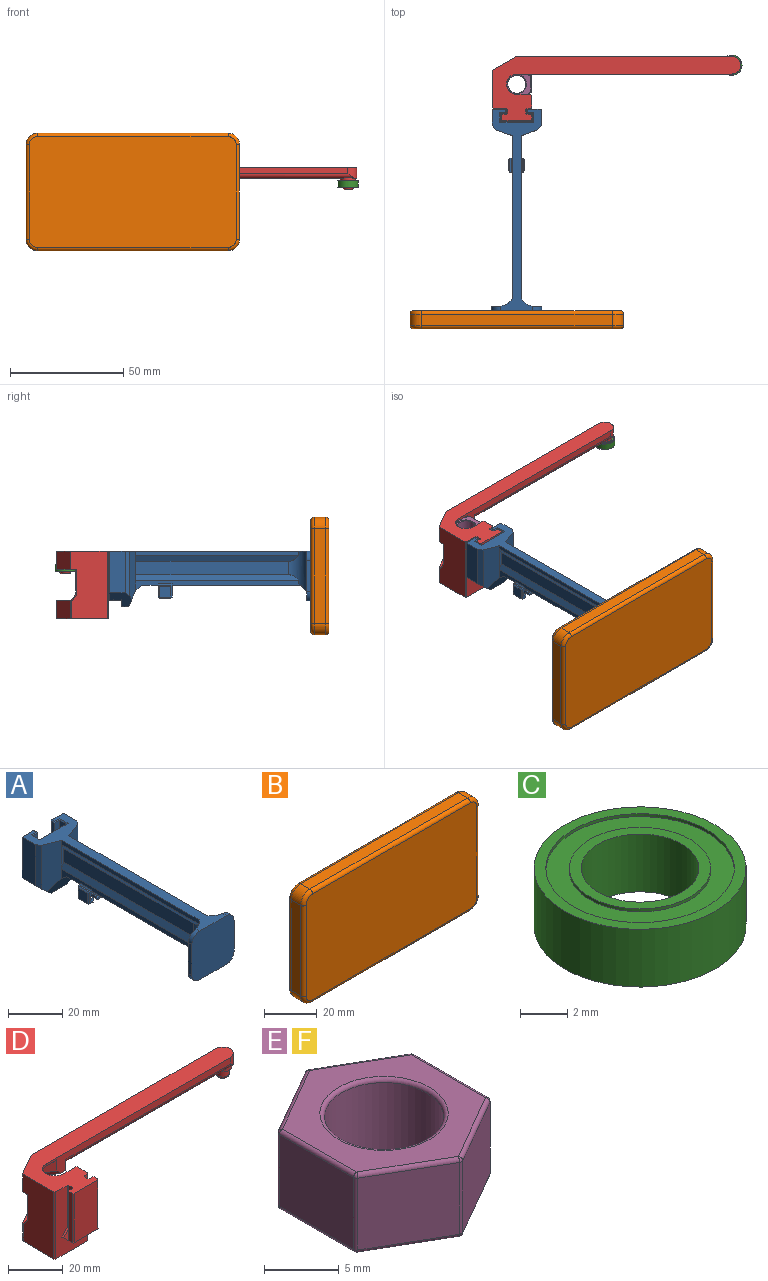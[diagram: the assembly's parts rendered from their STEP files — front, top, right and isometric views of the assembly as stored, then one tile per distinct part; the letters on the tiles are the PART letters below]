
ASSEMBLY  parts=6 mates=3
PART A: 121 faces, bbox 22x89x24.5 mm
  f0: plane 6.2x5.8mm, normal (0,1,0), area 14mm2, adj f3,f5,f7,f45,f47,f65,f70,f75
  f1: plane 6.2x5.8mm, normal (0,-1,0), area 14mm2, adj f2,f3,f5,f45,f47,f68,f73,f78
  f2: plane 57.05x5.58mm, normal (0,0,-1), area 228.9mm2, adj f1,f3,f5,f62,f63,f115
  f3: plane 72.07x4.42mm, normal (-1,0,0), area 139.2mm2, adj f0,f1,f2,f7,f13,f41,f62,f114
  f4: plane 72.07x1.92mm, normal (-1,0,0), area 138.5mm2, adj f10,f13,f40,f62
  f5: plane 72.07x4.42mm, normal (1,0,0), area 139.2mm2, adj f0,f1,f2,f7,f14,f38,f63,f113
  f6: plane 72.07x1.92mm, normal (1,0,0), area 138.5mm2, adj f10,f14,f39,f63
  f7: plane 7x4mm, normal (0,0,-1), area 28mm2, adj f0,f3,f5,f116
  f8: plane 11.16x1.4mm, normal (0,-1,0), area 12mm2, adj f13,f29,f40,f41
  f9: plane 21.83x6.44mm, normal (0,1,0), area 130.2mm2, adj f10,f12,f22,f26,f37,f118
  f10: plane 89.02x21.6mm, normal (0,0,1), area 483.4mm2, adj f4,f6,f9,f11,f12,f13,f14,f15
  f11: plane 21.83x6.44mm, normal (0,1,0), area 130.2mm2, adj f10,f15,f18,f25,f31,f117
  f12: plane 18.5x6.97mm, normal (-1,0,0), area 129mm2, adj f9,f10,f118,f120
  f13: plane 21.68x7.39mm, normal (-0.34,-0.94,0), area 156.6mm2, adj f3,f4,f8,f10,f64,f118,f120
  f14: plane 21.68x7.39mm, normal (0.34,-0.94,0), area 156.6mm2, adj f5,f6,f10,f27,f64,f117,f119
  f15: plane 18.5x6.97mm, normal (1,0,0), area 129mm2, adj f10,f11,f117,f119
  f16: plane 8.2x3.05mm, normal (0,0,-1), area 25mm2, adj f19,f64,f117,f118
  f17: plane 22x22mm, normal (0,-1,0), area 470.3mm2, adj f10,f42,f43,f44,f58,f59,f60,f61
  f18: plane 5.42x3mm, normal (-0.74,0,-0.67), area 7.4mm2, adj f11,f19,f23,f24,f25,f117
  f19: plane 24.1x14.17mm, normal (0,1,0), area 333mm2, adj f16,f18,f21,f23,f26,f34,f117,f118
  f20: plane 21.41x2.71mm, normal (0,-1,0), area 54mm2, adj f21,f22,f26,f36
  f21: plane 21.41x3.61mm, normal (1,0,0), area 77.3mm2, adj f19,f20,f26,f35
  f22: plane 18.43x1.81mm, normal (1,0,0), area 33.4mm2, adj f9,f20,f26,f37
  f23: plane 21.41x3.61mm, normal (-1,0,0), area 77.3mm2, adj f18,f19,f24,f33
  f24: plane 21.41x2.71mm, normal (0,-1,0), area 54mm2, adj f18,f23,f25,f32
  f25: plane 18.43x1.81mm, normal (-1,0,0), area 33.4mm2, adj f11,f18,f24,f31
  f26: plane 5.42x3mm, normal (0.74,0,-0.67), area 7.4mm2, adj f9,f19,f20,f21,f22,f118
  f27: plane 11.16x1.4mm, normal (0,-1,0), area 12mm2, adj f14,f30,f38,f39
  f28: plane 22x21.67mm, normal (0,1,0), area 161mm2, adj f42,f43,f44,f58,f59,f60,f61,f62
  f29: plane 67.55x6mm, normal (-1,0,0), area 405.3mm2, adj f8,f40,f41,f62
  f30: plane 67.55x6mm, normal (1,0,0), area 405.3mm2, adj f27,f38,f39,f63
  f31: plane 1.81x0.4mm, normal (-0.71,0,0.71), area 0.9mm2, adj f10,f11,f25,f32
  f32: plane 3.11x0.4mm, normal (0,-0.71,0.71), area 1.5mm2, adj f10,f24,f31,f33
  f33: plane 4.41x0.4mm, normal (-0.71,0,0.71), area 2.3mm2, adj f10,f23,f32,f34
  f34: plane 14.94x0.4mm, normal (0,0.71,0.71), area 8.2mm2, adj f10,f19,f33,f35
  f35: plane 4.41x0.4mm, normal (0.71,0,0.71), area 2.3mm2, adj f10,f21,f34,f36
  f36: plane 3.11x0.4mm, normal (0,-0.71,0.71), area 1.5mm2, adj f10,f20,f35,f37
  f37: plane 1.81x0.4mm, normal (0.71,0,0.71), area 0.9mm2, adj f9,f10,f22,f36
  f38: plane 72.07x2.58mm, normal (0.88,0,0.48), area 207.2mm2, adj f5,f27,f30,f63
  f39: plane 72.07x2.58mm, normal (0.88,0,-0.48), area 207.2mm2, adj f6,f27,f30,f63
  f40: plane 72.07x2.58mm, normal (-0.88,0,-0.48), area 207.2mm2, adj f4,f8,f29,f62
  f41: plane 72.07x2.58mm, normal (-0.88,0,0.48), area 207.2mm2, adj f3,f8,f29,f62
  f42: plane 14x1.8mm, normal (0,0,-1), area 25.2mm2, adj f17,f28,f59,f61
  f43: plane 14x1.8mm, normal (1,0,0), area 25.2mm2, adj f17,f28,f60,f61
  f44: plane 14x1.8mm, normal (-1,0,0), area 25.2mm2, adj f17,f28,f58,f59
  f45: plane 6x0.6mm, normal (0,0,1), area 3.6mm2, adj f0,f1,f66,f113
  f46: plane 5x4.8mm, normal (1,0,0), area 24mm2, adj f65,f66,f68,f69
  f47: plane 6x0.6mm, normal (0,0,1), area 3.6mm2, adj f0,f1,f90,f114
  f48: plane 5x4.8mm, normal (-1,0,0), area 24mm2, adj f85,f90,f95,f96
  f49: plane 5x1.75mm, normal (0,0,-1), area 8.8mm2, adj f94,f95,f105,f106
  f50: plane 5x1mm, normal (1,0,0), area 5mm2, adj f51,f93,f105,f111
  f51: plane 5x0.75mm, normal (0,0,1), area 3.8mm2, adj f50,f100,f108,f112
  f52: plane 5x1.8mm, normal (1,0,0), area 9mm2, adj f98,f99,f107,f108
  f53: plane 5x3.2mm, normal (0,0,-1), area 16mm2, adj f87,f88,f97,f98
  f54: plane 5x1.8mm, normal (-1,0,0), area 9mm2, adj f81,f82,f86,f87
  f55: plane 5x0.75mm, normal (0,0,1), area 3.8mm2, adj f56,f77,f80,f81
  f56: plane 5x1mm, normal (-1,0,0), area 5mm2, adj f55,f74,f75,f78
  f57: plane 5x1.75mm, normal (0,0,-1), area 8.8mm2, adj f69,f70,f73,f74
  f58: cylinder r=4mm len=4mm, axis (0,1,0), area 11.4mm2, adj f10,f17,f28,f44,f62
  f59: cylinder r=4mm len=4mm, axis (0,1,0), area 11.3mm2, adj f17,f28,f42,f44
  f60: cylinder r=4mm len=4mm, axis (0,-1,0), area 11.4mm2, adj f10,f17,f28,f43,f63
  f61: cylinder r=4mm len=4mm, axis (0,-1,0), area 11.3mm2, adj f17,f28,f42,f43
  f62: cylinder r=8mm len=18mm, axis (0,0,-1), area 166.3mm2, adj f2,f3,f4,f10,f28,f29,f40,f41
  f63: cylinder r=8mm len=18mm, axis (0,0,1), area 166.3mm2, adj f2,f5,f6,f10,f28,f30,f38,f39
  f64: plane 14.5x7mm, normal (0,-0.91,-0.42), area 77.7mm2, adj f13,f14,f16,f116,f117,f118
  f65: plane 5.3x0.5mm, normal (0.71,0.71,0), area 3.6mm2, adj f0,f46,f66,f67
  f66: plane 6x0.5mm, normal (0.71,0,0.71), area 3.9mm2, adj f45,f46,f65,f68
  f67: plane 0.5x0.5mm, normal (0.58,0.58,-0.58), area 0.2mm2, adj f65,f69,f70
  f68: plane 5.3x0.5mm, normal (0.71,-0.71,0), area 3.6mm2, adj f1,f46,f66,f71
  f69: plane 5x0.5mm, normal (0.71,0,-0.71), area 3.5mm2, adj f46,f57,f67,f71
  f70: plane 1.75x0.5mm, normal (0,0.71,-0.71), area 1.2mm2, adj f0,f57,f67,f72
  f71: plane 0.5x0.5mm, normal (0.58,-0.58,-0.58), area 0.2mm2, adj f68,f69,f73
  f72: plane 0.5x0.5mm, normal (-0.58,0.58,-0.58), area 0.2mm2, adj f70,f74,f75
  f73: plane 1.75x0.5mm, normal (0,-0.71,-0.71), area 1.2mm2, adj f1,f57,f71,f76
  f74: plane 5x0.5mm, normal (-0.71,0,-0.71), area 3.5mm2, adj f56,f57,f72,f76
  f75: plane 1x0.5mm, normal (-0.71,0.71,0), area 0.5mm2, adj f0,f56,f72,f77
  f76: plane 0.5x0.5mm, normal (-0.58,-0.58,-0.58), area 0.2mm2, adj f73,f74,f78
  f77: plane 0.75x0.5mm, normal (0,0.71,0.71), area 0.4mm2, adj f0,f55,f75,f79
  f78: plane 1x0.5mm, normal (-0.71,-0.71,0), area 0.5mm2, adj f1,f56,f76,f80
  f79: plane 1x1mm, normal (-0.58,0.58,0.58), area 0.6mm2, adj f0,f77,f81,f82
  f80: plane 0.75x0.5mm, normal (0,-0.71,0.71), area 0.4mm2, adj f1,f55,f78,f83
  f81: plane 5x0.5mm, normal (-0.71,0,0.71), area 3.5mm2, adj f54,f55,f79,f83
  f82: plane 1.8x0.5mm, normal (-0.71,0.71,0), area 1.3mm2, adj f0,f54,f79,f84
  f83: plane 1x1mm, normal (-0.58,-0.58,0.58), area 0.6mm2, adj f1,f80,f81,f86
  f84: plane 1x1mm, normal (-0.58,0.58,-0.58), area 0.6mm2, adj f0,f82,f87,f88
  f85: plane 5.3x0.5mm, normal (-0.71,0.71,0), area 3.6mm2, adj f0,f48,f89,f90
  f86: plane 1.8x0.5mm, normal (-0.71,-0.71,0), area 1.3mm2, adj f1,f54,f83,f91
  f87: plane 5x0.5mm, normal (-0.71,0,-0.71), area 3.5mm2, adj f53,f54,f84,f91
  f88: plane 3.2x0.5mm, normal (0,0.71,-0.71), area 2.3mm2, adj f0,f53,f84,f92
  f89: plane 0.5x0.5mm, normal (-0.58,0.58,-0.58), area 0.2mm2, adj f85,f94,f95
  f90: plane 6x0.5mm, normal (-0.71,0,0.71), area 3.9mm2, adj f47,f48,f85,f96
  f91: plane 1x1mm, normal (-0.58,-0.58,-0.58), area 0.6mm2, adj f1,f86,f87,f97
  f92: plane 1x1mm, normal (0.58,0.58,-0.58), area 0.6mm2, adj f0,f88,f98,f99
  f93: plane 1x0.5mm, normal (0.71,0.71,0), area 0.5mm2, adj f0,f50,f100,f101
  f94: plane 1.75x0.5mm, normal (0,0.71,-0.71), area 1.2mm2, adj f0,f49,f89,f101
  f95: plane 5x0.5mm, normal (-0.71,0,-0.71), area 3.5mm2, adj f48,f49,f89,f102
  f96: plane 5.3x0.5mm, normal (-0.71,-0.71,0), area 3.6mm2, adj f1,f48,f90,f102
  f97: plane 3.2x0.5mm, normal (0,-0.71,-0.71), area 2.3mm2, adj f1,f53,f91,f103
  f98: plane 5x0.5mm, normal (0.71,0,-0.71), area 3.5mm2, adj f52,f53,f92,f103
  f99: plane 1.8x0.5mm, normal (0.71,0.71,0), area 1.3mm2, adj f0,f52,f92,f104
  f100: plane 0.75x0.5mm, normal (0,0.71,0.71), area 0.4mm2, adj f0,f51,f93,f104
  f101: plane 0.5x0.5mm, normal (0.58,0.58,-0.58), area 0.2mm2, adj f93,f94,f105
  f102: plane 0.5x0.5mm, normal (-0.58,-0.58,-0.58), area 0.2mm2, adj f95,f96,f106
  f103: plane 1x1mm, normal (0.58,-0.58,-0.58), area 0.6mm2, adj f1,f97,f98,f107
  f104: plane 1x1mm, normal (0.58,0.58,0.58), area 0.6mm2, adj f0,f99,f100,f108
  f105: plane 5x0.5mm, normal (0.71,0,-0.71), area 3.5mm2, adj f49,f50,f101,f109
  f106: plane 1.75x0.5mm, normal (0,-0.71,-0.71), area 1.2mm2, adj f1,f49,f102,f109
  f107: plane 1.8x0.5mm, normal (0.71,-0.71,0), area 1.3mm2, adj f1,f52,f103,f110
  f108: plane 5x0.5mm, normal (0.71,0,0.71), area 3.5mm2, adj f51,f52,f104,f110
  f109: plane 0.5x0.5mm, normal (0.58,-0.58,-0.58), area 0.2mm2, adj f105,f106,f111
  f110: plane 1x1mm, normal (0.58,-0.58,0.58), area 0.6mm2, adj f1,f107,f108,f112
  f111: plane 1x0.5mm, normal (0.71,-0.71,0), area 0.5mm2, adj f1,f50,f109,f112
  f112: plane 0.75x0.5mm, normal (0,-0.71,0.71), area 0.4mm2, adj f1,f51,f110,f111
  f113: plane 6x0.5mm, normal (0.71,0,0.71), area 4.2mm2, adj f0,f1,f5,f45
  f114: plane 6x0.5mm, normal (-0.71,0,0.71), area 4.2mm2, adj f0,f1,f3,f47
  f115: plane 17.2x3mm, normal (0,0.77,-0.64), area 35.8mm2, adj f2,f28,f62,f63
  f116: plane 4x3mm, normal (0,-0.64,-0.77), area 15.6mm2, adj f3,f5,f7,f64
  f117: plane 9.76x6.7mm, normal (0.67,0,-0.74), area 58.8mm2, adj f11,f14,f15,f16,f18,f19,f64,f119
  f118: plane 9.76x6.7mm, normal (-0.67,0,-0.74), area 58.8mm2, adj f9,f12,f13,f16,f19,f26,f64,f120
  f119: plane 19.76x2.01mm, normal (0.82,-0.57,0), area 47mm2, adj f10,f14,f15,f117
  f120: plane 19.76x2.01mm, normal (-0.82,-0.57,0), area 47mm2, adj f10,f12,f13,f118
PART B: 26 faces, bbox 95.2x8x52.8 mm
  f0: plane 84.38x5mm, normal (0,0,-1), area 421.9mm2, adj f6,f9,f15,f24
  f1: plane 41.96x5mm, normal (1,0,0), area 209.8mm2, adj f6,f7,f16,f23
  f2: plane 84.38x5mm, normal (0,0,1), area 421.9mm2, adj f7,f8,f12,f19
  f3: plane 41.96x5mm, normal (-1,0,0), area 209.8mm2, adj f8,f9,f11,f20
  f4: plane 91.38x48.96mm, normal (0,-1,0), area 4463.7mm2, adj f10,f11,f12,f13,f14,f15,f16,f17
  f5: plane 91.38x48.96mm, normal (0,1,0), area 4463.7mm2, adj f18,f19,f20,f21,f22,f23,f24,f25
  f6: cylinder r=5mm len=5mm, axis (0,-1,0), area 39.3mm2, adj f0,f1,f17,f25
  f7: cylinder r=5mm len=5mm, axis (0,1,0), area 39.3mm2, adj f1,f2,f14,f21
  f8: cylinder r=5mm len=5mm, axis (0,-1,0), area 39.3mm2, adj f2,f3,f10,f18
  f9: cylinder r=5mm len=5mm, axis (0,1,0), area 39.3mm2, adj f0,f3,f13,f22
  f10: torus R=3.5mm, axis (0,-1,0), area 16.5mm2, adj f4,f8,f11,f12
  f11: cylinder r=1.5mm len=41.96mm, axis (0,0,1), area 98.9mm2, adj f3,f4,f10,f13
  f12: cylinder r=1.5mm len=84.38mm, axis (1,0,0), area 198.8mm2, adj f2,f4,f10,f14
  f13: torus R=3.5mm, axis (0,-1,0), area 16.5mm2, adj f4,f9,f11,f15
  f14: torus R=3.5mm, axis (0,-1,0), area 16.5mm2, adj f4,f7,f12,f16
  f15: cylinder r=1.5mm len=84.38mm, axis (-1,0,0), area 198.8mm2, adj f0,f4,f13,f17
  f16: cylinder r=1.5mm len=41.96mm, axis (0,0,-1), area 98.9mm2, adj f1,f4,f14,f17
  f17: torus R=3.5mm, axis (0,-1,0), area 16.5mm2, adj f4,f6,f15,f16
  f18: torus R=3.5mm, axis (0,-1,0), area 16.5mm2, adj f5,f8,f19,f20
  f19: cylinder r=1.5mm len=84.38mm, axis (-1,0,0), area 198.8mm2, adj f2,f5,f18,f21
  f20: cylinder r=1.5mm len=41.96mm, axis (0,0,-1), area 98.9mm2, adj f3,f5,f18,f22
  f21: torus R=3.5mm, axis (0,-1,0), area 16.5mm2, adj f5,f7,f19,f23
  f22: torus R=3.5mm, axis (0,-1,0), area 16.5mm2, adj f5,f9,f20,f24
  f23: cylinder r=1.5mm len=41.96mm, axis (0,0,1), area 98.9mm2, adj f1,f5,f21,f25
  f24: cylinder r=1.5mm len=84.38mm, axis (1,0,0), area 198.8mm2, adj f0,f5,f22,f25
  f25: torus R=3.5mm, axis (0,-1,0), area 16.5mm2, adj f5,f6,f23,f24
PART C: 12 faces, bbox 9x9x3 mm
  f0: plane 8x8mm, normal (0,0,1), area 22mm2, adj f3,f9
  f1: plane 8x8mm, normal (0,0,-1), area 22mm2, adj f2,f7
  f2: cylinder r=4mm len=8mm, axis (0,0,-1), area 3.8mm2, adj f1,f6
  f3: cylinder r=4mm len=8mm, axis (0,0,-1), area 3.8mm2, adj f0,f5
  f4: cylinder r=4.5mm len=9mm, axis (0,0,-1), area 84.8mm2, adj f5,f6
  f5: plane 9x9mm, normal (0,0,1), area 13.4mm2, adj f3,f4
  f6: plane 9x9mm, normal (0,0,-1), area 13.4mm2, adj f2,f4
  f7: cylinder r=3mm len=6mm, axis (0,0,-1), area 2.8mm2, adj f1,f11
  f8: cylinder r=2.5mm len=5mm, axis (0,0,-1), area 47.1mm2, adj f10,f11
  f9: cylinder r=3mm len=6mm, axis (0,0,-1), area 2.8mm2, adj f0,f10
  f10: plane 6x6mm, normal (0,0,1), area 8.6mm2, adj f8,f9
  f11: plane 6x6mm, normal (0,0,-1), area 8.6mm2, adj f7,f8
PART D: 102 faces, bbox 109.6x28.3x30 mm
  f0: plane 30x16.3mm, normal (0,-1,0), area 252mm2, adj f1,f8,f62,f79,f80,f84,f93
  f1: plane 22.76x17.3mm, normal (0,0,-1), area 156.5mm2, adj f0,f3,f4,f23,f24,f25,f34,f35
  f2: plane 22x13.28mm, normal (0,-1,0), area 269.7mm2, adj f5,f6,f8,f62,f86,f87
  f3: plane 30x16.26mm, normal (-1,0,0), area 448.7mm2, adj f1,f8,f11,f18,f29,f84,f90,f91
  f4: plane 30x5.11mm, normal (1,0,0), area 88mm2, adj f1,f8,f29,f66,f67,f68,f69,f93
  f5: plane 5.91x3mm, normal (0.74,0,0.67), area 11.2mm2, adj f2,f42,f43,f44,f48,f62,f81,f82
  f6: plane 4.92x3mm, normal (-0.74,0,0.67), area 9.2mm2, adj f2,f45,f46,f47,f62,f80,f83,f85
  f7: plane 7.27x3.68mm, normal (1,0,0), area 12.9mm2, adj f18,f53,f61,f89,f101
  f8: plane 109.64x28.32mm, normal (0,0,1), area 1042.1mm2, adj f0,f2,f3,f4,f11,f17,f19,f20
  f9: plane 17.5x6.65mm, normal (0.5,0.87,0), area 134.4mm2, adj f10,f12,f21,f50
  f10: plane 17.5x7.68mm, normal (1,0,0), area 128.9mm2, adj f9,f15,f18,f21,f51,f92
  f11: plane 10.65x8mm, normal (-0.5,0.87,0), area 98.4mm2, adj f3,f8,f18,f55
  f12: plane 17.5x6.15mm, normal (0,1,0), area 107.6mm2, adj f9,f21,f49,f67
  f13: plane 6.65x4.72mm, normal (0.5,0.87,0), area 34.6mm2, adj f14,f31,f33,f38,f76,f78
  f14: plane 7.68x4.72mm, normal (1,0,0), area 34.6mm2, adj f13,f28,f33,f37,f77,f78
  f15: plane 7.34x6.5mm, normal (0.5,-0.87,0), area 50.5mm2, adj f10,f16,f18,f21,f74
  f16: plane 5.62x5.51mm, normal (-0.5,-0.87,0), area 29mm2, adj f15,f17,f21,f41,f73,f74
  f17: plane 95.09x8mm, normal (0,-1,0), area 295.5mm2, adj f8,f16,f18,f20,f41,f54,f73,f89
  f18: plane 21.3x8.96mm, normal (0,0,-1), area 79.4mm2, adj f3,f7,f10,f11,f15,f17,f22,f41
  f19: plane 6.15x1mm, normal (0,1,0), area 6.2mm2, adj f8,f20,f69,f71
  f20: cylinder r=4.5mm len=9mm, axis (0,0,1), area 14.1mm2, adj f8,f17,f19,f72
  f21: plane 15.36x12.8mm, normal (0,0,-1), area 60mm2, adj f9,f10,f12,f15,f16,f68,f71,f72
  f22: plane 11x3mm, normal (0,1,0), area 33mm2, adj f18,f52,f90,f92
  f23: plane 10.15x8mm, normal (-0.5,0.87,0), area 93.8mm2, adj f1,f29,f96,f97
  f24: plane 8x6.15mm, normal (0.5,0.87,0), area 56.8mm2, adj f1,f29,f97,f98
  f25: plane 8x3.17mm, normal (1,0,0), area 24.2mm2, adj f1,f29,f98,f99,f100
  f26: plane 6.15x6mm, normal (0,-1,0), area 9.4mm2, adj f27,f29,f32,f34,f63,f99
  f27: plane 5.51x5.22mm, normal (-0.5,-0.87,0), area 28.9mm2, adj f26,f28,f33,f35,f63,f75
  f28: plane 6.65x4.72mm, normal (0.5,-0.87,0), area 34.6mm2, adj f14,f27,f33,f36,f75,f77
  f29: plane 18.43x17.3mm, normal (0,0,1), area 96.9mm2, adj f3,f4,f23,f24,f25,f26,f30,f32
  f30: plane 6.15x6mm, normal (0,1,0), area 9.4mm2, adj f29,f31,f32,f40,f65,f94
  f31: plane 5.51x5.22mm, normal (-0.5,0.87,0), area 28.9mm2, adj f13,f30,f33,f39,f65,f76
  f32: cylinder r=4.5mm len=9mm, axis (0,0,1), area 14.1mm2, adj f26,f29,f30,f64
  f33: plane 15.36x11.29mm, normal (0,0,-1), area 49.8mm2, adj f13,f14,f27,f28,f31,f63,f64,f65
  f34: plane 2x1mm, normal (0,-0.89,-0.45), area 1.1mm2, adj f1,f26,f35,f100
  f35: plane 5.55x4.2mm, normal (-0.45,-0.77,-0.45), area 14mm2, adj f1,f27,f34,f75
  f36: plane 7.2x4.74mm, normal (0.45,-0.77,-0.45), area 17.3mm2, adj f1,f28,f75,f77
  f37: plane 8.32x2mm, normal (0.89,0,-0.45), area 17.3mm2, adj f1,f14,f77,f78
  f38: plane 7.2x4.74mm, normal (0.45,0.77,-0.45), area 17.3mm2, adj f1,f13,f76,f78
  f39: plane 5.55x4.2mm, normal (-0.45,0.77,-0.45), area 14mm2, adj f1,f31,f40,f76
  f40: plane 2x1mm, normal (0,0.89,-0.45), area 1.1mm2, adj f1,f30,f39,f95
  f41: plane 7.23x3.6mm, normal (-0.45,-0.77,-0.45), area 14.8mm2, adj f16,f17,f18,f74
  f42: plane 21.98x1.71mm, normal (1,0,0), area 37.6mm2, adj f5,f8,f87,f88
  f43: plane 19x1.71mm, normal (1,0,0), area 32.5mm2, adj f5,f8,f81,f82
  f44: plane 21.43x1.71mm, normal (0,1,0), area 35mm2, adj f5,f8,f81,f88
  f45: plane 21.98x1.71mm, normal (-1,0,0), area 37.6mm2, adj f6,f8,f85,f86
  f46: plane 21.43x1.71mm, normal (0,1,0), area 35mm2, adj f6,f8,f83,f85
  f47: plane 19x1.71mm, normal (-1,0,0), area 32.5mm2, adj f6,f8,f79,f83
  f48: plane 21.46x1.74mm, normal (0,-1,0), area 35.6mm2, adj f5,f8,f82,f93
  f49: plane 6.15x3mm, normal (0,0.83,0.55), area 21.2mm2, adj f12,f29,f50,f66
  f50: plane 7.19x4.99mm, normal (0.42,0.72,0.55), area 24.6mm2, adj f9,f29,f49,f51
  f51: plane 9.68x3.38mm, normal (0.83,0,0.55), area 29.3mm2, adj f10,f29,f50,f52,f92
  f52: plane 5.5x3.38mm, normal (0,0.83,0.55), area 16.3mm2, adj f22,f29,f51,f91,f92
  f53: plane 88.39x5.8mm, normal (0,0,-1), area 480.4mm2, adj f7,f54,f55,f56,f61,f101
  f54: cylinder r=3.9mm len=7.8mm, axis (0,0,1), area 58.2mm2, adj f8,f17,f53,f55,f101
  f55: plane 95.08x8mm, normal (0,1,0), area 491.3mm2, adj f8,f11,f53,f54,f61
  f56: cylinder r=3.25mm len=6.5mm, axis (0,0,1), area 22mm2, adj f53,f57,f101
  f57: plane 6.5x6.5mm, normal (0,0,-1), area 15.1mm2, adj f56,f58
  f58: cylinder r=2.4mm len=4.8mm, axis (0,0,1), area 45.2mm2, adj f57,f60
  f59: plane 2.8x2.8mm, normal (0,0,-1), area 6.2mm2, adj f60
  f60: torus R=1.4mm, axis (0,0,1), area 20.1mm2, adj f58,f59
  f61: plane 10.65x6.15mm, normal (0.25,0.43,-0.87), area 37.6mm2, adj f7,f18,f53,f55
  f62: plane 13.95x5.91mm, normal (0,0,-1), area 72.2mm2, adj f0,f2,f5,f6,f80,f93
  f63: plane 5.51x0.5mm, normal (0,-0.71,-0.71), area 3.6mm2, adj f26,f27,f33,f64
  f64: cone r=5mm half-angle=45deg, axis (0,0,-1), area 10.6mm2, adj f32,f33,f63,f65
  f65: plane 5.51x0.5mm, normal (0,0.71,-0.71), area 3.6mm2, adj f30,f31,f33,f64
  f66: plane 3x2.5mm, normal (0.71,0.59,0.39), area 2.5mm2, adj f4,f29,f49,f67
  f67: plane 18.15x0.5mm, normal (0.71,0.71,0), area 12.6mm2, adj f4,f12,f66,f68
  f68: plane 3.18x0.5mm, normal (0.71,0,-0.71), area 2.1mm2, adj f4,f21,f67,f70
  f69: plane 1x0.5mm, normal (0.71,0.71,0), area 0.7mm2, adj f4,f8,f19,f70
  f70: plane 0.5x0.5mm, normal (0.58,0.58,-0.58), area 0.2mm2, adj f68,f69,f71
  f71: plane 6.15x0.5mm, normal (0,0.71,-0.71), area 4.3mm2, adj f19,f21,f70,f72
  f72: cone r=5mm half-angle=45deg, axis (0,0,-1), area 10.6mm2, adj f20,f21,f71,f73
  f73: plane 5.51x0.5mm, normal (0,-0.71,-0.71), area 3.6mm2, adj f16,f17,f21,f72
  f74: plane 2x1.28mm, normal (0.03,-0.96,-0.26), area 1mm2, adj f15,f16,f18,f41
  f75: plane 2x1.15mm, normal (0,-0.87,-0.5), area 1mm2, adj f1,f27,f28,f35,f36
  f76: plane 2x1.15mm, normal (0,0.87,-0.5), area 1mm2, adj f1,f13,f31,f38,f39
  f77: plane 2x1.22mm, normal (0.75,-0.43,-0.5), area 1mm2, adj f1,f14,f28,f36,f37
  f78: plane 2x1.22mm, normal (0.75,0.43,-0.5), area 1mm2, adj f1,f13,f14,f37,f38
  f79: plane 19x0.5mm, normal (-0.71,-0.71,0), area 13.4mm2, adj f0,f8,f47,f80
  f80: plane 3.4x3.19mm, normal (-0.52,-0.71,0.48), area 3mm2, adj f0,f6,f62,f79
  f81: plane 19.55x0.5mm, normal (0.71,0.71,0), area 13.6mm2, adj f5,f8,f43,f44
  f82: plane 19.55x0.5mm, normal (0.71,-0.71,0), area 13.6mm2, adj f5,f8,f43,f48
  f83: plane 19.55x0.5mm, normal (-0.71,0.71,0), area 13.6mm2, adj f6,f8,f46,f47
  f84: plane 30x0.5mm, normal (-0.71,-0.71,0), area 21.2mm2, adj f0,f1,f3,f8
  f85: plane 21.98x0.5mm, normal (-0.71,0.71,0), area 15.3mm2, adj f6,f8,f45,f46
  f86: plane 21.98x0.5mm, normal (-0.71,-0.71,0), area 15.3mm2, adj f2,f6,f8,f45
  f87: plane 21.98x0.5mm, normal (0.71,-0.71,0), area 15.3mm2, adj f2,f5,f8,f42
  f88: plane 21.98x0.5mm, normal (0.71,0.71,0), area 15.3mm2, adj f5,f8,f42,f44
  f89: plane 5x0.5mm, normal (0.71,-0.71,0), area 2.9mm2, adj f7,f17,f18,f101
  f90: plane 11.15x0.5mm, normal (-0.71,0.71,0), area 7.8mm2, adj f3,f18,f22,f91
  f91: plane 3x2.5mm, normal (-0.71,0.59,0.39), area 2.5mm2, adj f3,f29,f52,f90
  f92: plane 11x0.5mm, normal (0.71,0.71,0), area 7.6mm2, adj f10,f18,f22,f51,f52
  f93: plane 30x0.5mm, normal (0.71,-0.71,0), area 21mm2, adj f0,f1,f4,f5,f8,f48,f62
  f94: plane 6x0.5mm, normal (0.71,0.71,0), area 4.2mm2, adj f4,f29,f30,f95
  f95: plane 2.12x1.56mm, normal (0.71,0.63,-0.32), area 1.6mm2, adj f1,f4,f40,f94
  f96: plane 8x0.43mm, normal (-0.87,0.5,0), area 4mm2, adj f1,f3,f23,f29
  f97: plane 8x0.5mm, normal (0,1,0), area 4mm2, adj f1,f23,f24,f29
  f98: plane 8x0.43mm, normal (0.87,0.5,0), area 4mm2, adj f1,f24,f25,f29
  f99: plane 6x0.5mm, normal (0.71,-0.71,0), area 4.2mm2, adj f25,f26,f29,f100
  f100: plane 2.12x1.56mm, normal (0.71,-0.63,-0.32), area 1.6mm2, adj f1,f25,f34,f99
  f101: cylinder r=2mm len=88.35mm, axis (1,0,0), area 266.5mm2, adj f7,f17,f53,f54,f56,f89
PART E: 41 faces, bbox 12.8x14.7x6.5 mm
  f0: plane 6.1x5.9mm, normal (0.5,0.87,0), area 41.6mm2, adj f27,f32,f35,f38
  f1: plane 6.1x5.9mm, normal (-0.5,0.87,0), area 41.6mm2, adj f24,f33,f34,f38
  f2: plane 7.04x5.9mm, normal (-1,0,0), area 41.6mm2, adj f14,f23,f24,f25
  f3: plane 6.1x5.9mm, normal (-0.5,-0.87,0), area 41.6mm2, adj f9,f13,f14,f15
  f4: plane 6.1x5.9mm, normal (0.5,-0.87,0), area 41.6mm2, adj f9,f12,f16,f17
  f5: plane 7.04x5.9mm, normal (1,0,0), area 41.6mm2, adj f17,f22,f26,f27
  f6: cylinder r=4mm len=8mm, axis (0,0,-1), area 148.3mm2, adj f39,f40
  f7: plane 14.09x12.2mm, normal (0,0,1), area 70.8mm2, adj f12,f13,f22,f23,f32,f33,f40
  f8: plane 14.09x12.2mm, normal (0,0,-1), area 70.8mm2, adj f15,f16,f25,f26,f34,f35,f39
  f9: cylinder r=0.3mm len=5.9mm, axis (0,0,-1), area 1.9mm2, adj f3,f4,f10,f11
  f10: sphere r=0.3mm, area 0.1mm2, adj f9,f12,f13
  f11: sphere r=0.3mm, area 0.1mm2, adj f9,f15,f16
  f12: cylinder r=0.3mm len=6.25mm, axis (-0.87,-0.5,0), area 3.3mm2, adj f4,f7,f10,f18
  f13: cylinder r=0.3mm len=6.25mm, axis (-0.87,0.5,0), area 3.3mm2, adj f3,f7,f10,f19
  f14: cylinder r=0.3mm len=5.9mm, axis (0,0,-1), area 1.9mm2, adj f2,f3,f19,f20
  f15: cylinder r=0.3mm len=6.25mm, axis (0.87,-0.5,0), area 3.3mm2, adj f3,f8,f11,f20
  f16: cylinder r=0.3mm len=6.25mm, axis (0.87,0.5,0), area 3.3mm2, adj f4,f8,f11,f21
  f17: cylinder r=0.3mm len=5.9mm, axis (0,0,-1), area 1.9mm2, adj f4,f5,f18,f21
  f18: sphere r=0.3mm, area 0.1mm2, adj f12,f17,f22
  f19: sphere r=0.3mm, area 0.1mm2, adj f13,f14,f23
  f20: sphere r=0.3mm, area 0.1mm2, adj f14,f15,f25
  f21: sphere r=0.3mm, area 0.1mm2, adj f16,f17,f26
  f22: cylinder r=0.3mm len=7.04mm, axis (0,-1,0), area 3.3mm2, adj f5,f7,f18,f28
  f23: cylinder r=0.3mm len=7.04mm, axis (0,1,0), area 3.3mm2, adj f2,f7,f19,f29
  f24: cylinder r=0.3mm len=5.9mm, axis (0,0,-1), area 1.9mm2, adj f1,f2,f29,f30
  f25: cylinder r=0.3mm len=7.04mm, axis (0,-1,0), area 3.3mm2, adj f2,f8,f20,f30
  f26: cylinder r=0.3mm len=7.04mm, axis (0,1,0), area 3.3mm2, adj f5,f8,f21,f31
  f27: cylinder r=0.3mm len=5.9mm, axis (0,0,-1), area 1.9mm2, adj f0,f5,f28,f31
  f28: sphere r=0.3mm, area 0.1mm2, adj f22,f27,f32
  f29: sphere r=0.3mm, area 0.1mm2, adj f23,f24,f33
  f30: sphere r=0.3mm, area 0.1mm2, adj f24,f25,f34
  f31: sphere r=0.3mm, area 0.1mm2, adj f26,f27,f35
  f32: cylinder r=0.3mm len=6.25mm, axis (0.87,-0.5,0), area 3.3mm2, adj f0,f7,f28,f36
  f33: cylinder r=0.3mm len=6.25mm, axis (0.87,0.5,0), area 3.3mm2, adj f1,f7,f29,f36
  f34: cylinder r=0.3mm len=6.25mm, axis (-0.87,-0.5,0), area 3.3mm2, adj f1,f8,f30,f37
  f35: cylinder r=0.3mm len=6.25mm, axis (-0.87,0.5,0), area 3.3mm2, adj f0,f8,f31,f37
  f36: sphere r=0.3mm, area 0.1mm2, adj f32,f33,f38
  f37: sphere r=0.3mm, area 0.1mm2, adj f34,f35,f38
  f38: cylinder r=0.3mm len=5.9mm, axis (0,0,-1), area 1.9mm2, adj f0,f1,f36,f37
  f39: torus R=4.3mm, axis (0,0,1), area 12.2mm2, adj f6,f8
  f40: torus R=4.3mm, axis (0,0,1), area 12.2mm2, adj f6,f7
PART F: same geometry as E
PLACE A t=(-1.52,69.47,0.52)mm
PLACE B t=(-1.52,-30.53,-10.48)mm
PLACE C t=(167.18,78,-6.98)mm
PLACE D t=(-1.52,69.6,0.52)mm
PLACE E t=(1.98,69.6,-7.48)mm
PLACE F t=(1.98,69.6,-29.48)mm
MATE fastened C.f2 <-> D.f54  axis (0,0,1) through (93.57,78,-5.48)mm
MATE fastened A.f10 <-> D.f8  axis (0,0,1) through (-1.52,52.67,0.52)mm
MATE fastened B.f5 <-> A.f17  axis (0,1,0) through (-1.52,-30.53,-10.48)mm
